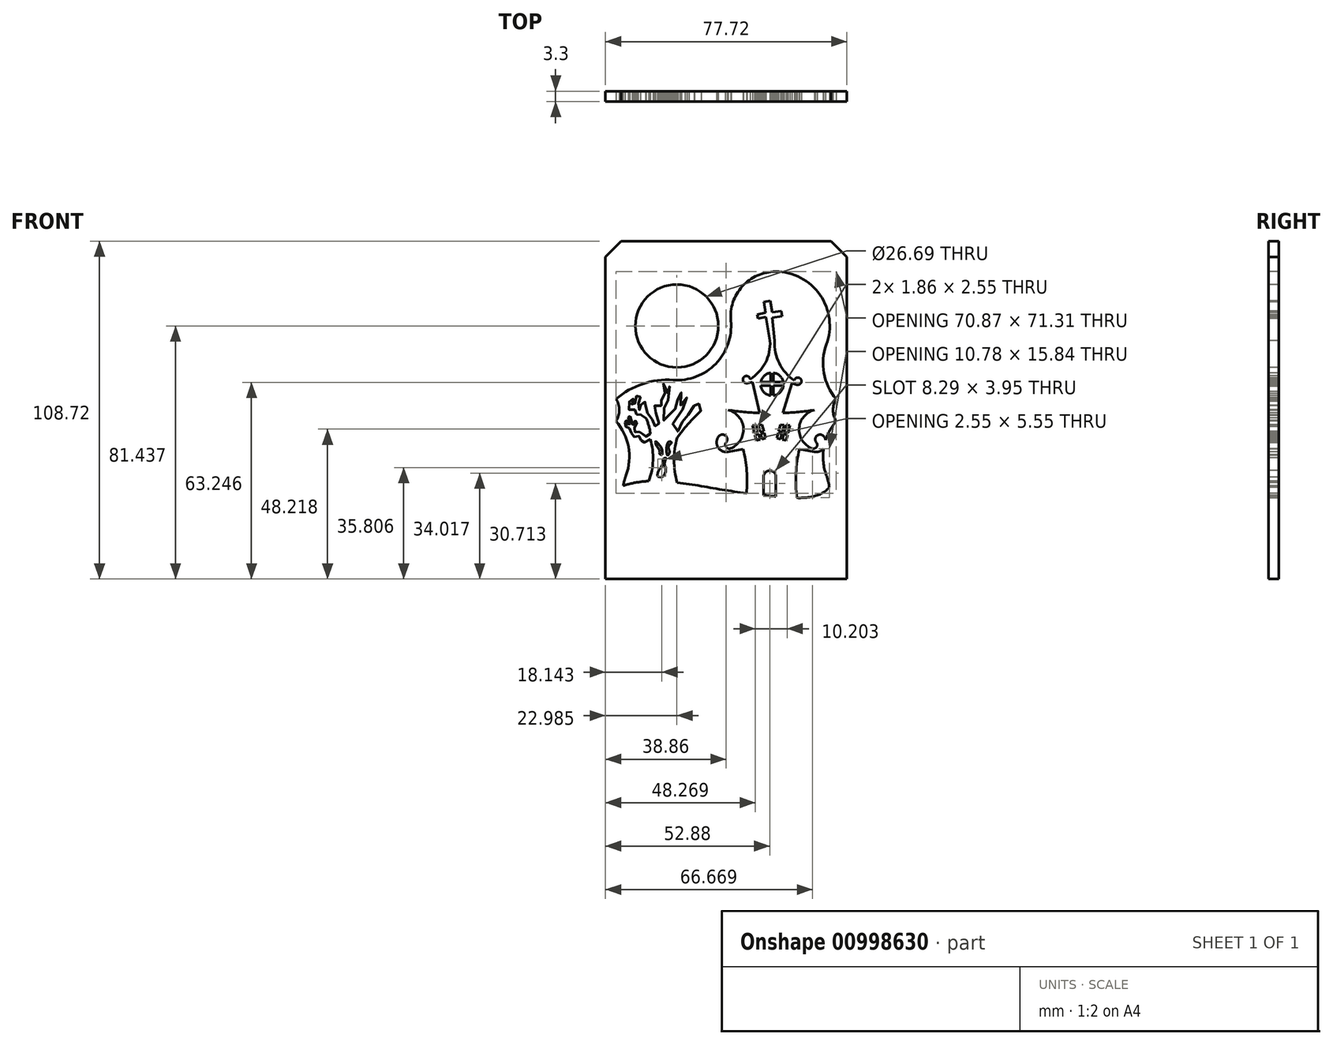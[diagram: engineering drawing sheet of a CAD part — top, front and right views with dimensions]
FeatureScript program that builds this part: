
annotation { "Feature Type Name" : "Feature", "Feature Type Description" : "" }
export const myFeature = defineFeature(function(context is Context, id is Id, definition is map)
    precondition{}
    {
        {
            var Q0;
            Q0=qCreatedBy(makeId("Front.planeOp"),FACE);
            var sketch = newSketch(context, id + "F0", { "sketchPlane" : qUnion([Q0])});
            skLineSegment(sketch, "E0.bottom", {"start": v(38.86, 54.36) * mm, "end": v(-38.86, 54.36) * mm});
            skLineSegment(sketch, "E0.top", {"start": v(38.86, -54.36) * mm, "end": v(-38.86, -54.36) * mm});
            skLineSegment(sketch, "E0.left", {"start": v(38.86, 54.36) * mm, "end": v(38.86, -54.36) * mm});
            skLineSegment(sketch, "E0.right", {"start": v(-38.86, 54.36) * mm, "end": v(-38.86, -54.36) * mm});
            skPoint(sketch, "E0.middle", {"position": v(0, 0) * mm});
            skSolve(sketch);
        }
        {
            var Q0;
            Q0=qSketchRegion(id+"F0",true);
            extrude(context, id + "F1", {"entities" : qUnion([Q0]), "depth" : 3.3 * mm});
        }
        {
            var Q0;
            Q0=makeQuery(id+"F1.opExtrude","CAP_FACE",FACE,{"disambiguationData":[OSD([sQuery(id+"F0.wireOp",EDGE,"E0.bottom"),sQuery(id+"F0.wireOp",EDGE,"E0.top"),sQuery(id+"F0.wireOp",EDGE,"E0.left"),sQuery(id+"F0.wireOp",EDGE,"E0.right")])],"isStart":false});
            var sketch = newSketch(context, id + "F2", { "sketchPlane" : qUnion([Q0])});
            skLineSegment(sketch, "E1", {"start": v(0, 57.24) * mm, "end": v(0, -57.24) * mm, "construction": true});
            skLineSegment(sketch, "E2", {"start": v(-50.8, 0) * mm, "end": v(50.8, 0) * mm, "construction": true});
            skArc(sketch, "E3", {"start": v(35.44, -3.57) * mm, "mid": v(31.46, -11.87) * mm, "end": v(32.26, -21.03) * mm});
            skLineSegment(sketch, "E4", {"start": v(15.88, -44.54) * mm, "end": v(0, -44.54) * mm, "construction": true});
            skArc(sketch, "E5", {"start": v(15.88, -44.54) * mm, "mid": v(30.2, -37.06) * mm, "end": v(32.26, -21.03) * mm});
            skArc(sketch, "E6", {"start": v(15.88, -44.54) * mm, "mid": v(7.78, -45.34) * mm, "end": v(0, -47.71) * mm});
            skArc(sketch, "E7.MirrorCS", {"start": v(-15.87, -44.54) * mm, "mid": v(-7.78, -45.34) * mm, "end": v(0, -47.71) * mm});
            skArc(sketch, "E8.MirrorCS", {"start": v(-15.87, -44.54) * mm, "mid": v(-30.2, -37.06) * mm, "end": v(-32.26, -21.03) * mm});
            skArc(sketch, "E9.MirrorCS", {"start": v(-35.44, -3.57) * mm, "mid": v(-31.46, -11.87) * mm, "end": v(-32.26, -21.03) * mm});
            skArc(sketch, "E10.MirrorCS", {"start": v(-35.44, 3.57) * mm, "mid": v(-31.46, 11.87) * mm, "end": v(-32.26, 21.03) * mm});
            skArc(sketch, "E11.MirrorCS", {"start": v(-15.88, 44.54) * mm, "mid": v(-30.2, 37.06) * mm, "end": v(-32.26, 21.03) * mm});
            skArc(sketch, "E12.MirrorCS", {"start": v(-15.88, 44.54) * mm, "mid": v(-7.78, 45.34) * mm, "end": v(0, 47.71) * mm});
            skArc(sketch, "E13.MirrorCS", {"start": v(15.87, 44.54) * mm, "mid": v(7.78, 45.34) * mm, "end": v(0, 47.71) * mm});
            skArc(sketch, "E14.MirrorCS", {"start": v(15.87, 44.54) * mm, "mid": v(30.2, 37.06) * mm, "end": v(32.26, 21.03) * mm});
            skArc(sketch, "E15.MirrorCS", {"start": v(35.44, 3.57) * mm, "mid": v(31.46, 11.87) * mm, "end": v(32.26, 21.03) * mm});
            skArc(sketch, "E16", {"start": v(35.44, 3.57) * mm, "mid": v(34.41, 0) * mm, "end": v(35.44, -3.57) * mm});
            skPoint(sketch, "E17.orphan", {"position": v(39.69, 0) * mm});
            skArc(sketch, "E18.MirrorCS", {"start": v(-35.44, 3.57) * mm, "mid": v(-34.41, 0) * mm, "end": v(-35.44, -3.57) * mm});
            skPoint(sketch, "E19.orphan", {"position": v(-39.69, 0) * mm});
            skSolve(sketch);
        }
        {
            var Q0;
            {var subQ7=sQuery(id+"F2.wireOp",EDGE,"E5");Q0=makeQuery(id+"F2.imprint","IMPRINT",FACE,{"disambiguationData":[TD([[makeQuery(id+"F2.imprint","IMPRINT",EDGE,{"derivedFrom":subQ7}),1.0]])]});}
            extrude(context, id + "F3", {"entities" : qUnion([Q0]), "operationType" : NewBodyOperationType.REMOVE, "endBound" : BoundingType.THROUGH_ALL, "oppositeDirection" : true, "depth" : 25.4 * mm});
        }
        {
            var Q0;
            Q0=makeQuery(id+"F2.imprint","IMPRINT",FACE,{"disambiguationData":[TD([[makeQuery(id+"F2.imprint","IMPRINT",EDGE,{"derivedFrom":sQuery(id+"F2.wireOp",EDGE,"E3")}),1.0]])]});
            var sketch = newSketch(context, id + "F4", { "sketchPlane" : qUnion([Q0])});
            skFitSpline(sketch, "E20", {"points": [v(-34.74, -25) * mm, v(-17.68, -23.14) * mm, v(0, -25.84) * mm, v(18.3, -28) * mm, v(33.6, -24.4) * mm], "startDerivative": vector(68.08, 28.42) * mm, "endDerivative": vector(41.75, 55.86) * mm});
            skArc(sketch, "E21.0", {"start": v(15.88, -44.54) * mm, "mid": v(28.97, -38.63) * mm, "end": v(33.2, -24.9) * mm});
            skArc(sketch, "E22.0", {"start": v(-15.87, -44.54) * mm, "mid": v(-29.14, -38.43) * mm, "end": v(-33.13, -24.38) * mm});
            skArc(sketch, "E23.0", {"start": v(15.88, -44.54) * mm, "mid": v(7.78, -45.34) * mm, "end": v(0, -47.71) * mm});
            skArc(sketch, "E23.1", {"start": v(-15.87, -44.54) * mm, "mid": v(-7.78, -45.34) * mm, "end": v(0, -47.71) * mm});
            skPoint(sketch, "E24.orphan", {"position": v(-32.26, -21.03) * mm});
            skLineSegment(sketch, "E25.bottom", {"start": v(23.58, -32.65) * mm, "end": v(5.44, -32.65) * mm, "construction": true});
            skLineSegment(sketch, "E25.top", {"start": v(23.58, -12.55) * mm, "end": v(5.44, -12.55) * mm, "construction": true});
            skLineSegment(sketch, "E25.left", {"start": v(23.58, -32.65) * mm, "end": v(23.58, -12.55) * mm, "construction": true});
            skLineSegment(sketch, "E25.right", {"start": v(5.44, -32.65) * mm, "end": v(5.44, -12.55) * mm, "construction": true});
            skArc(sketch, "E26", {"start": v(6.5, -26.77) * mm, "mid": v(6.6, -19.6) * mm, "end": v(5.44, -12.55) * mm});
            skArc(sketch, "E27", {"start": v(23.58, -12.55) * mm, "mid": v(22.47, -20.37) * mm, "end": v(22.78, -28.26) * mm});
            skLineSegment(sketch, "E28", {"start": v(0.57, -13.45) * mm, "end": v(5.44, -12.55) * mm});
            skLineSegment(sketch, "E29", {"start": v(28.46, 0) * mm, "end": v(0.57, 0) * mm, "construction": true});
            skArc(sketch, "E30", {"start": v(-2.4, -8.48) * mm, "mid": v(-2.65, -12) * mm, "end": v(0.57, -13.45) * mm});
            skArc(sketch, "E31", {"start": v(0, -10.42) * mm, "mid": v(-0.23, -8.24) * mm, "end": v(-2.4, -8.48) * mm});
            skArc(sketch, "E32", {"start": v(0, -10.42) * mm, "mid": v(-0.04, -11.92) * mm, "end": v(1.4, -12.35) * mm});
            skArc(sketch, "E33", {"start": v(1.4, -12.35) * mm, "mid": v(5.55, -5.86) * mm, "end": v(0.57, 0) * mm});
            skLineSegment(sketch, "E34", {"start": v(14.51, 0) * mm, "end": v(14.51, -12.55) * mm, "construction": true});
            skArc(sketch, "E35.MirrorCS", {"start": v(27.61, -12.35) * mm, "mid": v(23.47, -5.86) * mm, "end": v(28.46, 0) * mm});
            skLineSegment(sketch, "E36.MirrorCS", {"start": v(28.46, -13.45) * mm, "end": v(23.58, -12.55) * mm});
            skArc(sketch, "E37.MirrorCS", {"start": v(31.42, -8.48) * mm, "mid": v(31.67, -12) * mm, "end": v(28.46, -13.45) * mm});
            skArc(sketch, "E38.MirrorCS", {"start": v(29.02, -10.42) * mm, "mid": v(29.25, -8.24) * mm, "end": v(31.42, -8.48) * mm});
            skArc(sketch, "E39.MirrorCS", {"start": v(29.02, -10.42) * mm, "mid": v(29.06, -11.92) * mm, "end": v(27.61, -12.35) * mm});
            skArc(sketch, "E40", {"start": v(0.57, 0) * mm, "mid": v(5.65, -0.6) * mm, "end": v(10.76, -0.93) * mm});
            skLineSegment(sketch, "E41", {"start": v(10.76, -0.93) * mm, "end": v(8.47, 9.06) * mm});
            skLineSegment(sketch, "E42", {"start": v(8.47, 9.06) * mm, "end": v(6.8, 8.68) * mm});
            skArc(sketch, "E43", {"start": v(7.7, 9.94) * mm, "mid": v(5.6, 10.49) * mm, "end": v(6.8, 8.68) * mm});
            skLineSegment(sketch, "E44", {"start": v(14.51, 0) * mm, "end": v(14.77, 8.31) * mm, "construction": true});
            skLineSegment(sketch, "E45.MirrorCS", {"start": v(18.26, -0.93) * mm, "end": v(21.1, 8.66) * mm});
            skLineSegment(sketch, "E46.MirrorCS", {"start": v(21.1, 8.66) * mm, "end": v(22.75, 8.18) * mm});
            skArc(sketch, "E47.MirrorCS", {"start": v(21.93, 9.5) * mm, "mid": v(24.07, 9.9) * mm, "end": v(22.75, 8.18) * mm});
            skArc(sketch, "E48", {"start": v(7.7, 9.94) * mm, "mid": v(12.62, 15.22) * mm, "end": v(14.1, 22.28) * mm});
            skArc(sketch, "E49", {"start": v(15.59, 22.28) * mm, "mid": v(17.1, 15.06) * mm, "end": v(21.93, 9.5) * mm});
            skLineSegment(sketch, "E50", {"start": v(14.1, 22.28) * mm, "end": v(12.75, 29.94) * mm});
            skLineSegment(sketch, "E51", {"start": v(12.75, 29.94) * mm, "end": v(10.25, 29.5) * mm});
            skLineSegment(sketch, "E52", {"start": v(10.25, 29.5) * mm, "end": v(10.04, 30.72) * mm});
            skLineSegment(sketch, "E53", {"start": v(10.04, 30.72) * mm, "end": v(12.66, 31.3) * mm});
            skLineSegment(sketch, "E54", {"start": v(12.66, 31.3) * mm, "end": v(12.12, 34.79) * mm});
            skLineSegment(sketch, "E55", {"start": v(12.12, 34.79) * mm, "end": v(14.24, 35.11) * mm});
            skLineSegment(sketch, "E56", {"start": v(14.24, 35.11) * mm, "end": v(14.8, 31.45) * mm});
            skLineSegment(sketch, "E57", {"start": v(14.8, 31.45) * mm, "end": v(17.72, 31.9) * mm});
            skLineSegment(sketch, "E58", {"start": v(17.72, 31.9) * mm, "end": v(17.99, 30.17) * mm});
            skLineSegment(sketch, "E59", {"start": v(17.99, 30.17) * mm, "end": v(14.89, 29.68) * mm});
            skLineSegment(sketch, "E60", {"start": v(14.89, 29.68) * mm, "end": v(15.59, 22.28) * mm});
            skArc(sketch, "E61.trimOffspring", {"start": v(18.26, -0.93) * mm, "mid": v(23.37, -0.6) * mm, "end": v(28.46, 0) * mm});
            skPoint(sketch, "E62.orphan", {"position": v(18.2, -1.17) * mm});
            skLineSegment(sketch, "E63", {"start": v(8.48, -4.98) * mm, "end": v(9.12, -7.41) * mm});
            skLineSegment(sketch, "E64", {"start": v(9.77, -9.85) * mm, "end": v(10.94, -9.54) * mm});
            skLineSegment(sketch, "E65", {"start": v(12.72, -9.06) * mm, "end": v(12.26, -7.34) * mm});
            skLineSegment(sketch, "E66", {"start": v(11.56, -4.7) * mm, "end": v(10.33, -4.82) * mm});
            skLineSegment(sketch, "E67", {"start": v(9.75, -4.87) * mm, "end": v(10.34, -7.13) * mm});
            skLineSegment(sketch, "E68", {"start": v(10.34, -7.13) * mm, "end": v(9.12, -7.41) * mm});
            skLineSegment(sketch, "E69", {"start": v(10.33, -4.82) * mm, "end": v(10.9, -7.06) * mm});
            skLineSegment(sketch, "E70", {"start": v(10.9, -7.06) * mm, "end": v(12.14, -6.89) * mm});
            skLineSegment(sketch, "E71", {"start": v(9.29, -8.05) * mm, "end": v(10.46, -7.73) * mm});
            skLineSegment(sketch, "E72", {"start": v(10.46, -7.73) * mm, "end": v(10.94, -9.54) * mm});
            skLineSegment(sketch, "E73", {"start": v(11.57, -9.37) * mm, "end": v(11.12, -7.64) * mm});
            skLineSegment(sketch, "E74", {"start": v(11.12, -7.64) * mm, "end": v(12.26, -7.34) * mm});
            skLineSegment(sketch, "E75.trimOffspring", {"start": v(12.14, -6.89) * mm, "end": v(11.56, -4.7) * mm});
            skLineSegment(sketch, "E76.trimOffspring", {"start": v(9.75, -4.87) * mm, "end": v(8.48, -4.98) * mm});
            skLineSegment(sketch, "E77.trimOffspring", {"start": v(9.29, -8.05) * mm, "end": v(9.77, -9.85) * mm});
            skLineSegment(sketch, "E78.trimOffspring", {"start": v(11.57, -9.37) * mm, "end": v(12.72, -9.06) * mm});
            skLineSegment(sketch, "E79.MirrorCS", {"start": v(17.46, -4.7) * mm, "end": v(18.69, -4.82) * mm});
            skLineSegment(sketch, "E80.MirrorCS", {"start": v(19.27, -4.87) * mm, "end": v(18.68, -7.13) * mm});
            skLineSegment(sketch, "E81.MirrorCS", {"start": v(17.45, -9.37) * mm, "end": v(17.9, -7.64) * mm});
            skLineSegment(sketch, "E82.MirrorCS", {"start": v(18.68, -7.13) * mm, "end": v(19.9, -7.41) * mm});
            skLineSegment(sketch, "E83.MirrorCS", {"start": v(17.9, -7.64) * mm, "end": v(16.76, -7.34) * mm});
            skLineSegment(sketch, "E84.MirrorCS", {"start": v(18.69, -4.82) * mm, "end": v(18.12, -7.06) * mm});
            skLineSegment(sketch, "E85.MirrorCS", {"start": v(16.88, -6.89) * mm, "end": v(17.46, -4.7) * mm});
            skLineSegment(sketch, "E86.MirrorCS", {"start": v(18.12, -7.06) * mm, "end": v(16.88, -6.89) * mm});
            skLineSegment(sketch, "E87.MirrorCS", {"start": v(19.27, -4.87) * mm, "end": v(20.54, -4.98) * mm});
            skLineSegment(sketch, "E88.MirrorCS", {"start": v(20.54, -4.98) * mm, "end": v(19.9, -7.41) * mm});
            skLineSegment(sketch, "E89.MirrorCS", {"start": v(19.73, -8.05) * mm, "end": v(18.56, -7.73) * mm});
            skLineSegment(sketch, "E90.MirrorCS", {"start": v(19.73, -8.05) * mm, "end": v(19.25, -9.85) * mm});
            skLineSegment(sketch, "E91.MirrorCS", {"start": v(19.25, -9.85) * mm, "end": v(18.08, -9.54) * mm});
            skLineSegment(sketch, "E92.MirrorCS", {"start": v(18.56, -7.73) * mm, "end": v(18.08, -9.54) * mm});
            skLineSegment(sketch, "E93.MirrorCS", {"start": v(17.45, -9.37) * mm, "end": v(16.3, -9.06) * mm});
            skLineSegment(sketch, "E94.MirrorCS", {"start": v(16.3, -9.06) * mm, "end": v(16.76, -7.34) * mm});
            skArc(sketch, "E95", {"start": v(14.28, 11.97) * mm, "mid": v(12.23, 10.98) * mm, "end": v(11.15, 8.98) * mm});
            skLineSegment(sketch, "E96", {"start": v(14.28, 11.97) * mm, "end": v(14.28, 8.98) * mm});
            skLineSegment(sketch, "E97", {"start": v(15.17, 4.65) * mm, "end": v(15.17, 7.88) * mm});
            skLineSegment(sketch, "E98", {"start": v(18.4, 8.98) * mm, "end": v(15.17, 8.98) * mm});
            skLineSegment(sketch, "E99", {"start": v(11.1, 7.88) * mm, "end": v(14.28, 7.88) * mm});
            skLineSegment(sketch, "E100.trimOffspring", {"start": v(15.17, 8.98) * mm, "end": v(15.17, 11.98) * mm});
            skLineSegment(sketch, "E101.trimOffspring", {"start": v(15.17, 7.88) * mm, "end": v(18.43, 7.88) * mm});
            skLineSegment(sketch, "E102.trimOffspring", {"start": v(14.28, 7.88) * mm, "end": v(14.28, 4.66) * mm});
            skLineSegment(sketch, "E103.trimOffspring", {"start": v(14.28, 8.98) * mm, "end": v(11.15, 8.98) * mm});
            skArc(sketch, "E104.trimOffspring", {"start": v(11.1, 7.88) * mm, "mid": v(12.14, 5.73) * mm, "end": v(14.28, 4.66) * mm});
            skArc(sketch, "E105.trimOffspring", {"start": v(18.4, 8.98) * mm, "mid": v(17.28, 11.01) * mm, "end": v(15.17, 11.98) * mm});
            skArc(sketch, "E106.trimOffspring", {"start": v(15.17, 4.65) * mm, "mid": v(17.37, 5.7) * mm, "end": v(18.43, 7.88) * mm});
            skLineSegment(sketch, "E107.left", {"start": v(12.04, -27.4) * mm, "end": v(12.04, -21.48) * mm});
            skLineSegment(sketch, "E107.right", {"start": v(16, -27.8) * mm, "end": v(16, -21.48) * mm});
            skArc(sketch, "E108", {"start": v(16, -21.48) * mm, "mid": v(14.02, -19.5) * mm, "end": v(12.04, -21.48) * mm});
            skLineSegment(sketch, "E109", {"start": v(12.04, -27.4) * mm, "end": v(16, -27.8) * mm});
            skArc(sketch, "E110.0", {"start": v(-35.44, -3.57) * mm, "mid": v(-31.46, -11.87) * mm, "end": v(-32.26, -21.03) * mm, "construction": true});
            skArc(sketch, "E110.1", {"start": v(15.87, 44.54) * mm, "mid": v(7.78, 45.34) * mm, "end": v(0, 47.71) * mm});
            skArc(sketch, "E110.2", {"start": v(-15.88, 44.54) * mm, "mid": v(-30.2, 37.06) * mm, "end": v(-32.26, 21.03) * mm, "construction": true});
            skArc(sketch, "E110.3", {"start": v(-35.44, 3.57) * mm, "mid": v(-34.41, 0) * mm, "end": v(-35.44, -3.57) * mm, "construction": true});
            skArc(sketch, "E110.4", {"start": v(-35.44, 3.57) * mm, "mid": v(-31.46, 11.87) * mm, "end": v(-32.26, 21.03) * mm});
            skArc(sketch, "E110.5", {"start": v(-15.88, 44.54) * mm, "mid": v(-7.78, 45.34) * mm, "end": v(0, 47.71) * mm});
            skArc(sketch, "E111", {"start": v(-17.1, 9.66) * mm, "mid": v(-3.37, 14.89) * mm, "end": v(1.5, 28.74) * mm});
            skArc(sketch, "E112", {"start": v(-17.1, 9.66) * mm, "mid": v(-26.87, 8.42) * mm, "end": v(-35.44, 3.57) * mm});
            skArc(sketch, "E113", {"start": v(15.87, 44.54) * mm, "mid": v(5.2, 39.82) * mm, "end": v(1.5, 28.74) * mm});
            skArc(sketch, "E114.trimOffspring", {"start": v(-15.88, 44.54) * mm, "mid": v(-30.2, 37.06) * mm, "end": v(-32.26, 21.03) * mm});
            skArc(sketch, "E115", {"start": v(-24.92, -22.89) * mm, "mid": v(-23.55, -16.2) * mm, "end": v(-24.4, -9.44) * mm});
            skFitSpline(sketch, "E116", {"points": [v(-24.4, -9.44) * mm, v(-26.98, -10.38) * mm, v(-27.97, -8.39) * mm, v(-29.93, -8.52) * mm, v(-30.92, -6) * mm, v(-32.1, -5.52) * mm, v(-32.53, -4.18) * mm, v(-32.18, -3.27) * mm, v(-31.84, -4.44) * mm, v(-31.05, -4.83) * mm, v(-31.49, -2) * mm, v(-30.88, -2.14) * mm, v(-30.1, -5.05) * mm, v(-29.45, -3.57) * mm, v(-28.71, -3.66) * mm, v(-29.54, -5.78) * mm, v(-29.23, -7.17) * mm, v(-27.54, -7.04) * mm, v(-26.28, -8.52) * mm, v(-24.4, -7.6) * mm], "startDerivative": vector(-46.53, -30.94) * mm, "endDerivative": vector(36.03, 29.74) * mm});
            skArc(sketch, "E117", {"start": v(-24.4, -7.6) * mm, "mid": v(-24.93, -4.98) * mm, "end": v(-25.9, -2.49) * mm});
            skFitSpline(sketch, "E118", {"points": [v(-25.9, -2.49) * mm, v(-27.5, -1.49) * mm, v(-28.76, -1.49) * mm, v(-29.23, 0) * mm, v(-31.14, 0) * mm, v(-30.8, 3.42) * mm, v(-29.97, 3.55) * mm, v(-30.27, 1.77) * mm, v(-29.54, 1.72) * mm, v(-28.8, 4.59) * mm, v(-27.67, 4.37) * mm, v(-28.28, 1.98) * mm, v(-27.84, 0) * mm, v(-27.2, 2.46) * mm, v(-25.9, 2.37) * mm, v(-25.9, 0) * mm, v(-24.11, -2.49) * mm, v(-22.72, -5.26) * mm, v(-21.68, -4.18) * mm, v(-23.16, 1.33) * mm, v(-20.82, 1.46) * mm, v(-20.82, 3.02) * mm], "startDerivative": vector(-33.14, 31.82) * mm, "endDerivative": vector(-15.18, 49.9) * mm});
            skFitSpline(sketch, "E119", {"points": [v(-20.82, 3.02) * mm, v(-19.2, 3.92) * mm, v(-20.04, 5.84) * mm, v(-20.82, 8.3) * mm, v(-20.04, 8.38) * mm, v(-19.62, 6.46) * mm, v(-18.62, 5.34) * mm, v(-18.96, 7.3) * mm, v(-18.2, 7.55) * mm, v(-18.12, 4.13) * mm, v(-19.33, 2.25) * mm, v(-19.46, 0.87) * mm, v(-20.82, 0) * mm, v(-20.04, -3.35) * mm, v(-16.32, 0) * mm, v(-17.1, 1.46) * mm, v(-15.74, 3.02) * mm, v(-15.45, 5.84) * mm, v(-14.49, 5.55) * mm, v(-14.82, 3.02) * mm, v(-14.53, 1.46) * mm, v(-13.36, 4) * mm, v(-12.02, 3.02) * mm, v(-14.2, 0) * mm, v(-17.1, -4.06) * mm, v(-17.1, -7.4) * mm, v(-14.36, -5.44) * mm, v(-14.57, -4.1) * mm, v(-12.78, -3.22) * mm, v(-12.53, -1.68) * mm, v(-10.44, -0.8) * mm, v(-10.27, 1.46) * mm, v(-9.35, 0) * mm, v(-8.6, 3.02) * mm, v(-8.1, 0) * mm, v(-9.44, -1.26) * mm, v(-11.31, -3.26) * mm, v(-13.15, -4.6) * mm, v(-13.36, -6.6) * mm, v(-15.78, -8.94) * mm], "startDerivative": vector(94.65, 30.69) * mm, "endDerivative": vector(-102.82, -69.25) * mm});
            skArc(sketch, "E120", {"start": v(-15.78, -8.94) * mm, "mid": v(-16.8, -16.14) * mm, "end": v(-15.78, -23.34) * mm});
            skFitSpline(sketch, "E121", {"points": [v(-22.4, -11.55) * mm, v(-21.43, -13.07) * mm, v(-21.4, -14.11) * mm, v(-20.72, -14.36) * mm, v(-20.54, -13.59) * mm, v(-20.94, -12.02) * mm, v(-21.71, -11.06) * mm, v(-22.67, -10.07) * mm, v(-22.4, -11.55) * mm]});
            skFitSpline(sketch, "E122", {"points": [v(-18.38, -10.1) * mm, v(-19.09, -11.5) * mm, v(-19.21, -12.7) * mm, v(-19.15, -14.02) * mm, v(-18.84, -14.6) * mm, v(-18.38, -14.05) * mm, v(-18.26, -13.1) * mm, v(-18.56, -12.32) * mm, v(-18.29, -11.28) * mm, v(-17.6, -10.38) * mm, v(-18.38, -10.1) * mm]});
            skFitSpline(sketch, "E123", {"points": [v(-20.3, -15.78) * mm, v(-20.35, -17.1) * mm, v(-20.9, -18.47) * mm, v(-21.8, -19.67) * mm, v(-21.9, -21.46) * mm, v(-20.45, -21.43) * mm, v(-19.64, -20.38) * mm, v(-19.43, -18.84) * mm, v(-19.7, -17.85) * mm, v(-19.7, -16.37) * mm, v(-19.43, -15.38) * mm, v(-20.3, -15.78) * mm]});
            skCircle(sketch, "E124", {"center": v(-15.88, 27.08) * mm, "radius": 13.34 * mm});
            skSolve(sketch);
        }
        {
            var Q0;
            Q0=qSketchRegion(id+"F4",true);
            extrude(context, id + "F5", {"entities" : qUnion([Q0]), "operationType" : NewBodyOperationType.ADD, "oppositeDirection" : true, "depth" : 3.3 * mm});
        }
        {
            var Q0;
            Q0=makeQuery(id+"F1.opExtrude","SWEPT_EDGE",EDGE,{"disambiguationData":[OSD([sQuery(id+"F0.wireOp",EDGE,"E0.bottom"),sQuery(id+"F0.wireOp",EDGE,"E0.right")])]});
            var Q1;
            Q1=makeQuery(id+"F1.opExtrude","SWEPT_EDGE",EDGE,{"disambiguationData":[OSD([sQuery(id+"F0.wireOp",EDGE,"E0.bottom"),sQuery(id+"F0.wireOp",EDGE,"E0.left")])]});
            chamfer(context, id + "F6", {"entities" : qUnion([Q0, Q1]), "width" : 5.08 * mm, "tangentPropagation" : true});
        }
    });
